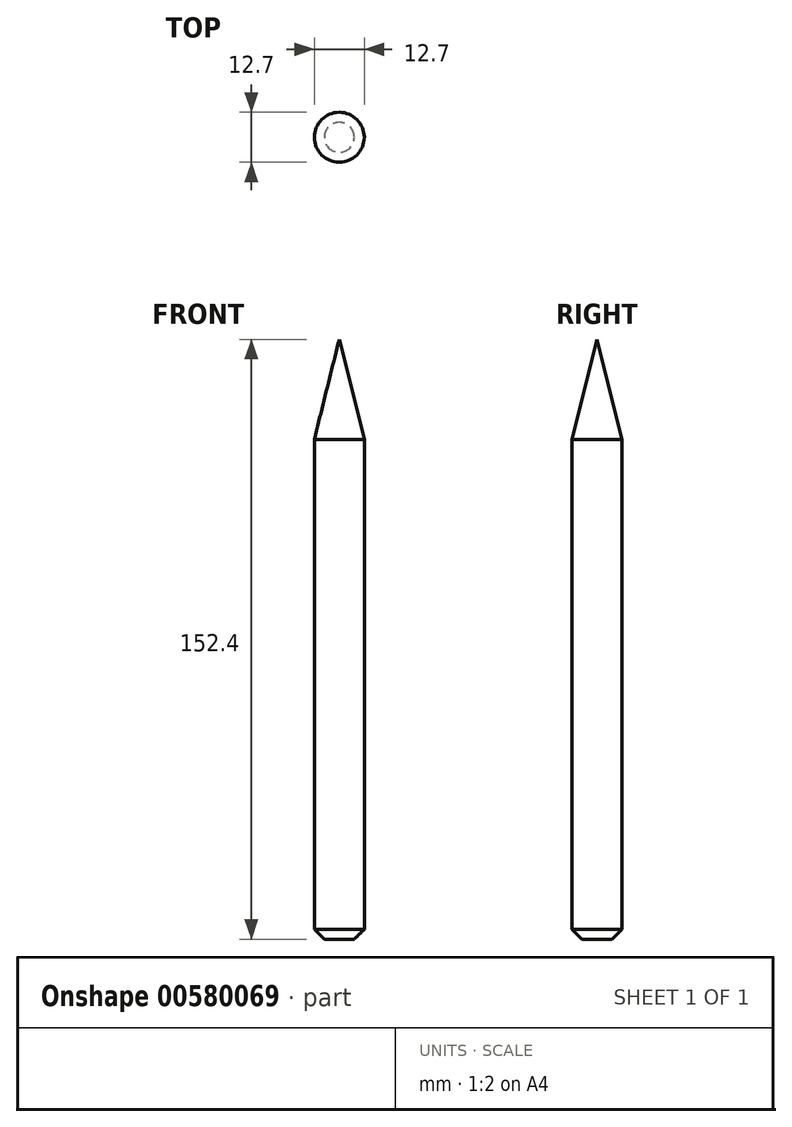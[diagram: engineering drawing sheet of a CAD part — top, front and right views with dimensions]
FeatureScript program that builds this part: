
annotation { "Feature Type Name" : "Feature", "Feature Type Description" : "" }
export const myFeature = defineFeature(function(context is Context, id is Id, definition is map)
    precondition{}
    {
        {
            var Q0;
            Q0=qCreatedBy(makeId("Front.planeOp"),FACE);
            var sketch = newSketch(context, id + "F0", { "sketchPlane" : qUnion([Q0])});
            skLineSegment(sketch, "E0", {"start": v(0, 152.4) * mm, "end": v(0, 0) * mm});
            skLineSegment(sketch, "E1", {"start": v(0, 0) * mm, "end": v(6.35, 0) * mm});
            skLineSegment(sketch, "E2", {"start": v(6.35, 0) * mm, "end": v(6.35, 127) * mm});
            skLineSegment(sketch, "E3", {"start": v(6.35, 127) * mm, "end": v(0, 152.4) * mm});
            skSolve(sketch);
        }
        {
            var Q0;
            Q0 = qSketchRegion(id + "F0", true);
            var Q1;
            Q1=sQuery(id+"F0.wireOp",EDGE,"E0");
            revolve(context, id + "F1", {"entities" : qUnion([Q0]), "axis" : qUnion([Q1]), "revolveType" : RevolveType.FULL});
        }
        {
            var Q0;
            Q0=makeQuery(id+"F1.opRevolve","SWEPT_EDGE",EDGE,{"disambiguationData":[OSD([sQuery(id+"F0.wireOp",EDGE,"E1"),sQuery(id+"F0.wireOp",EDGE,"E2")])]});
            chamfer(context, id + "F2", {"entities" : qUnion([Q0]), "width" : 2.54 * mm, "tangentPropagation" : true});
        }
    });
